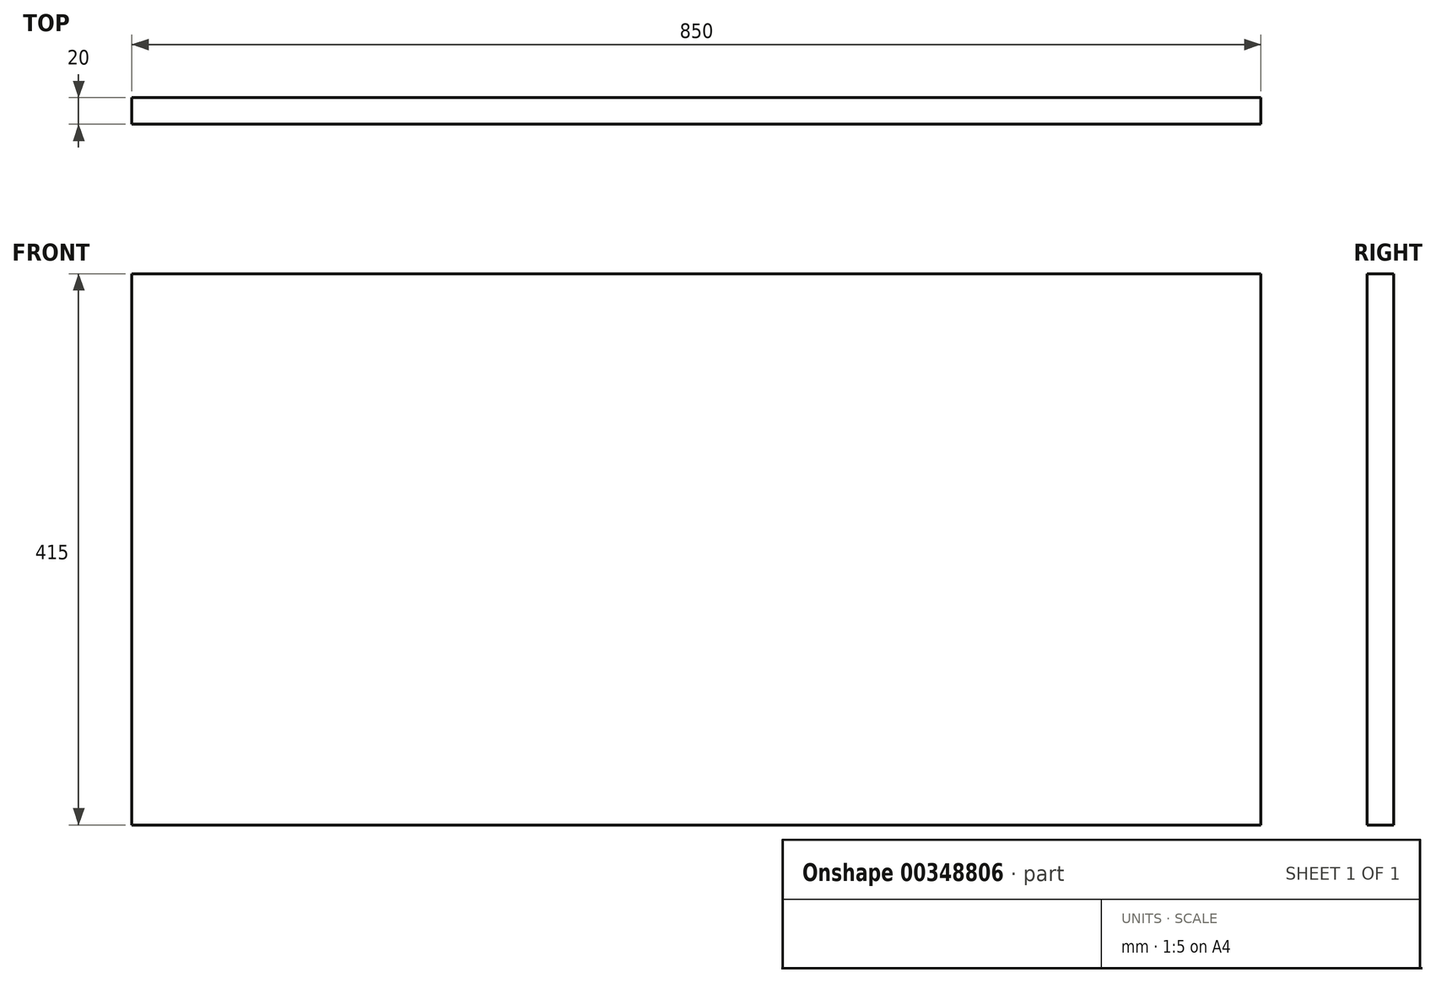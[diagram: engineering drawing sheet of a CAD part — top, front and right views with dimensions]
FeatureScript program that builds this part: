
annotation { "Feature Type Name" : "Feature", "Feature Type Description" : "" }
export const myFeature = defineFeature(function(context is Context, id is Id, definition is map)
    precondition{}
    {
        {
            var Q0;
            Q0=qCreatedBy(makeId("Front.planeOp"),FACE);
            var sketch = newSketch(context, id + "F0", { "sketchPlane" : qUnion([Q0])});
            skLineSegment(sketch, "E0.bottom", {"start": v(-850, -415) * mm, "end": v(0, -415) * mm});
            skLineSegment(sketch, "E0.top", {"start": v(-850, 0) * mm, "end": v(0, 0) * mm});
            skLineSegment(sketch, "E0.left", {"start": v(-850, -415) * mm, "end": v(-850, 0) * mm});
            skLineSegment(sketch, "E0.right", {"start": v(0, -415) * mm, "end": v(0, 0) * mm});
            skSolve(sketch);
        }
        {
            var Q0;
            Q0=qSketchRegion(id+"F0",true);
            extrude(context, id + "F1", {"entities" : qUnion([Q0]), "depth" : 20 * mm});
        }
    });
